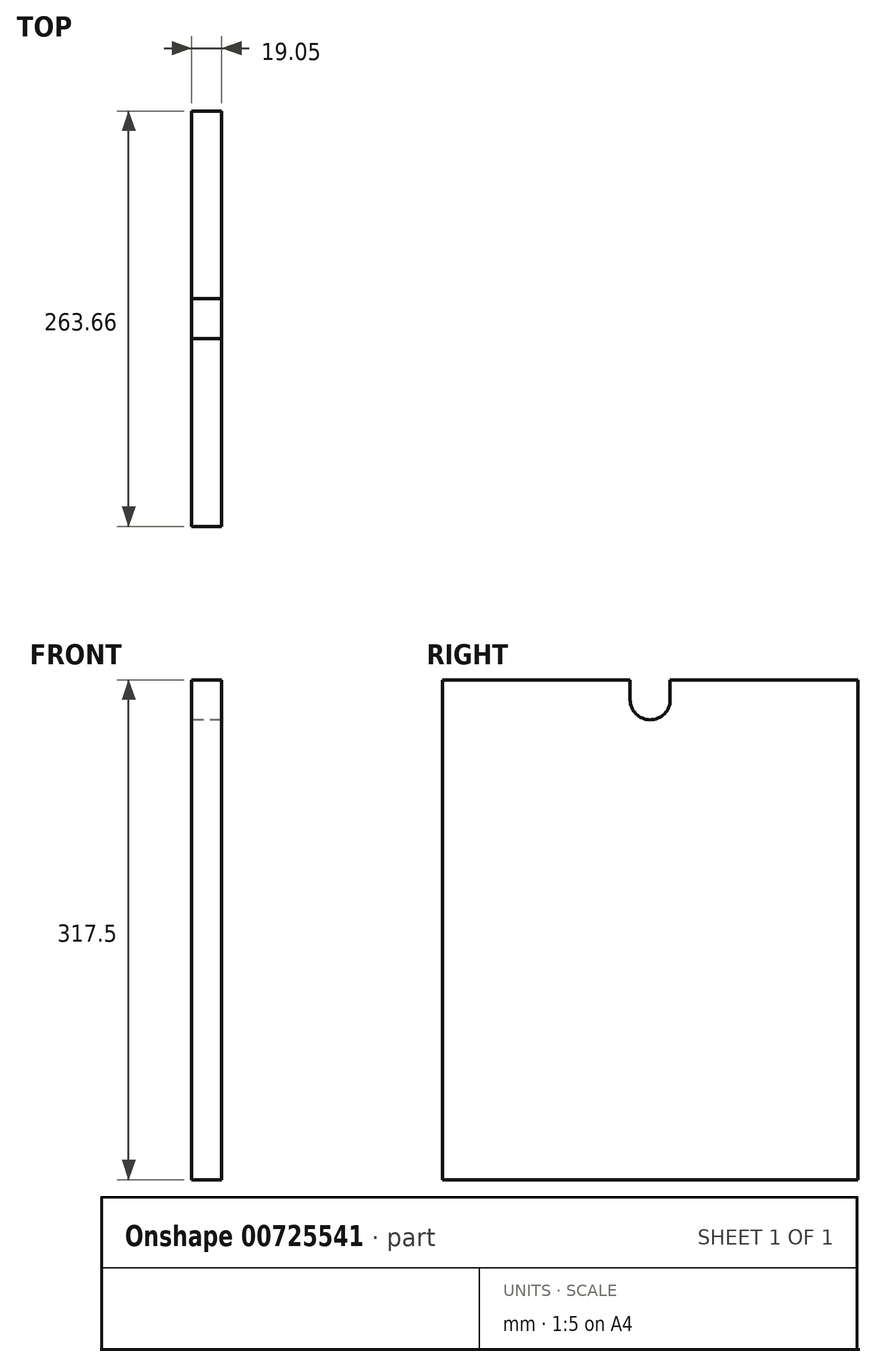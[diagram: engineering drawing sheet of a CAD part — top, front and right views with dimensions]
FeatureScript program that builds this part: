
annotation { "Feature Type Name" : "Feature", "Feature Type Description" : "" }
export const myFeature = defineFeature(function(context is Context, id is Id, definition is map)
    precondition{}
    {
        {
            var Q0;
            Q0=qCreatedBy(makeId("Right.planeOp"),FACE);
            var sketch = newSketch(context, id + "F0", { "sketchPlane" : qUnion([Q0])});
            skLineSegment(sketch, "E0.bottom", {"start": v(131.83, 158.75) * mm, "end": v(-131.83, 158.75) * mm});
            skLineSegment(sketch, "E0.top", {"start": v(131.83, -158.75) * mm, "end": v(-131.83, -158.75) * mm});
            skLineSegment(sketch, "E0.left", {"start": v(131.83, 158.75) * mm, "end": v(131.83, -158.75) * mm});
            skLineSegment(sketch, "E0.right", {"start": v(-131.83, 158.75) * mm, "end": v(-131.83, -158.75) * mm});
            skPoint(sketch, "E0.middle", {"position": v(0, 0) * mm});
            skCircle(sketch, "E1", {"center": v(0, 146.05) * mm, "radius": 12.7 * mm});
            skLineSegment(sketch, "E2", {"start": v(12.7, 146.05) * mm, "end": v(12.7, 158.75) * mm});
            skLineSegment(sketch, "E3", {"start": v(-12.7, 146.05) * mm, "end": v(-12.7, 158.75) * mm});
            skSolve(sketch);
        }
        {
            var Q0;
            Q0=makeQuery(id+"F0.imprint","IMPRINT",FACE,{"disambiguationData":[TD([[makeQuery(id+"F0.imprint","IMPRINT",EDGE,{"derivedFrom":sQuery(id+"F0.wireOp",EDGE,"E0.top")}),-1.0]])]});
            extrude(context, id + "F1", {"entities" : qUnion([Q0]), "depth" : 19.05 * mm, "offsetDistance" : 25.4 * mm});
        }
    });
